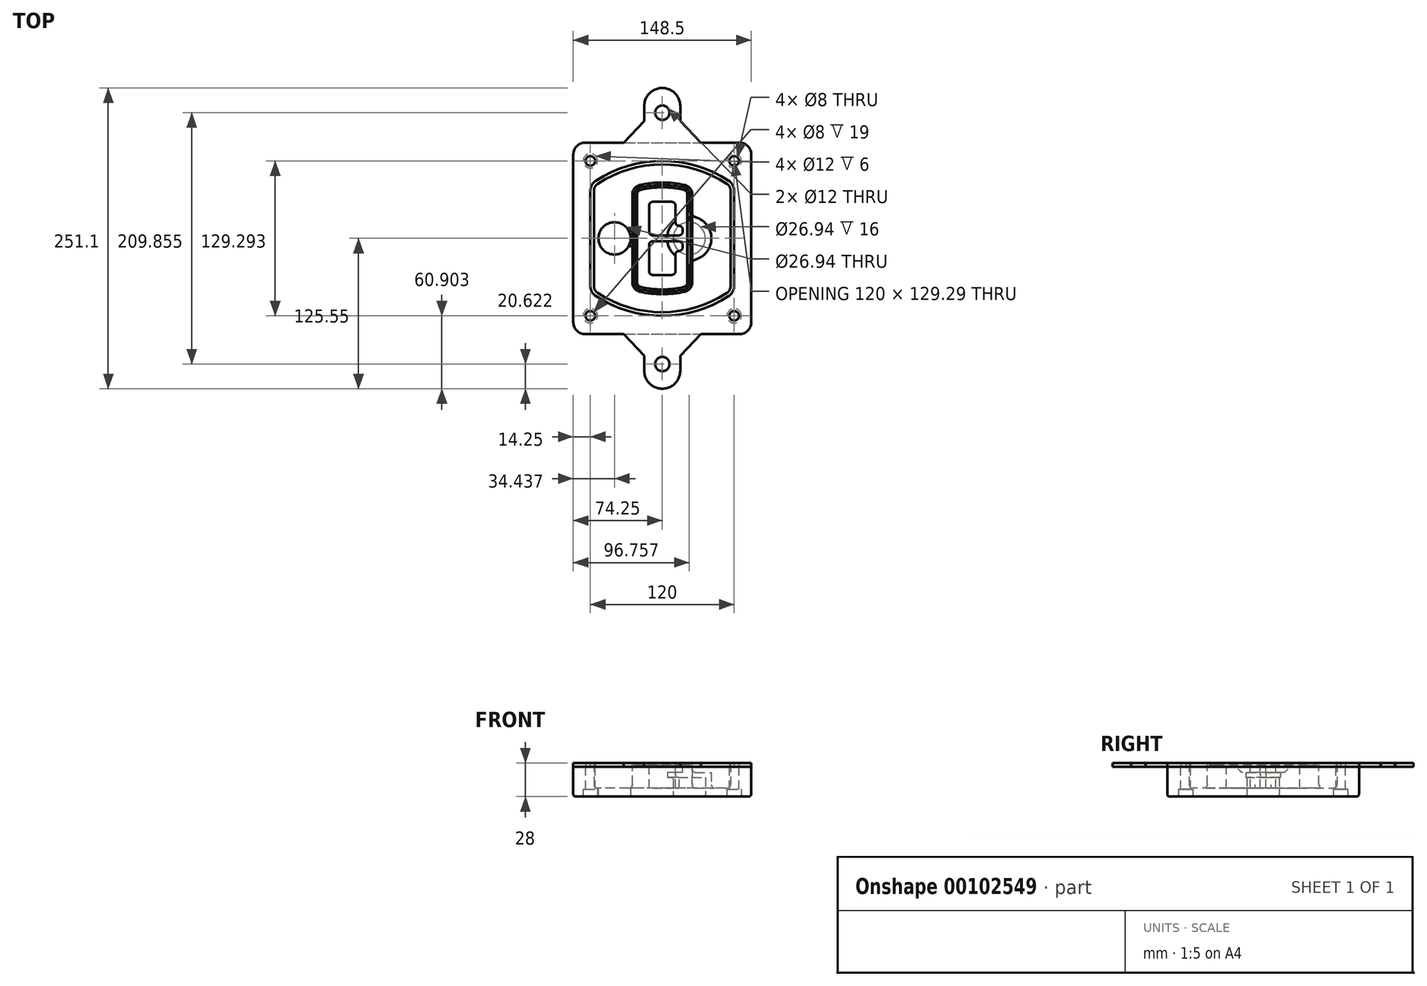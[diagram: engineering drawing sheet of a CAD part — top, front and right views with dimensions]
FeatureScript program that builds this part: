
annotation { "Feature Type Name" : "Feature", "Feature Type Description" : "" }
export const myFeature = defineFeature(function(context is Context, id is Id, definition is map)
    precondition{}
    {
        {
            var Q0;
            Q0=qCreatedBy(makeId("Top.planeOp"),FACE);
            var sketch = newSketch(context, id + "F0", { "sketchPlane" : qUnion([Q0])});
            skPoint(sketch, "E0.rect.middle", {"position": v(0, 0) * mm});
            skLineSegment(sketch, "E1.bottom", {"start": v(-64.25, -80) * mm, "end": v(64.25, -80) * mm});
            skLineSegment(sketch, "E1.top", {"start": v(-64.25, 80) * mm, "end": v(64.25, 80) * mm});
            skLineSegment(sketch, "E1.left", {"start": v(-74.25, -70) * mm, "end": v(-74.25, 70) * mm});
            skLineSegment(sketch, "E1.right", {"start": v(74.25, -70) * mm, "end": v(74.25, 70) * mm});
            skLineSegment(sketch, "E2", {"start": v(-74.25, 80) * mm, "end": v(74.25, -80) * mm, "construction": true});
            skLineSegment(sketch, "E3", {"start": v(74.25, 80) * mm, "end": v(-74.25, -80) * mm, "construction": true});
            skCircle(sketch, "E4", {"center": v(-60, 64.65) * mm, "radius": 4 * mm});
            skCircle(sketch, "E5", {"center": v(60, 64.65) * mm, "radius": 4 * mm});
            skCircle(sketch, "E6", {"center": v(60, -64.65) * mm, "radius": 4 * mm});
            skCircle(sketch, "E7", {"center": v(-60, -64.65) * mm, "radius": 4 * mm});
            skLineSegment(sketch, "E8", {"start": v(-60, 64.65) * mm, "end": v(60, 64.65) * mm, "construction": true});
            skLineSegment(sketch, "E9", {"start": v(60, 64.65) * mm, "end": v(60, -64.65) * mm, "construction": true});
            skLineSegment(sketch, "E10", {"start": v(60, -64.65) * mm, "end": v(-60, -64.65) * mm, "construction": true});
            skLineSegment(sketch, "E11", {"start": v(-60, -64.65) * mm, "end": v(-60, 64.65) * mm, "construction": true});
            skLineSegment(sketch, "E12", {"start": v(-60, 39.77) * mm, "end": v(-60, -39.77) * mm});
            skLineSegment(sketch, "E13", {"start": v(60, 39.77) * mm, "end": v(60, -39.77) * mm});
            skArc(sketch, "E14", {"start": v(55.47, 48.14) * mm, "mid": v(0, 64.65) * mm, "end": v(-55.47, 48.14) * mm});
            skArc(sketch, "E15", {"start": v(-55.47, -48.14) * mm, "mid": v(0, -64.65) * mm, "end": v(55.47, -48.14) * mm});
            skLineSegment(sketch, "E16", {"start": v(-60, 0) * mm, "end": v(60, 0) * mm, "construction": true});
            skPoint(sketch, "E17.visualSharp", {"position": v(-60, -45) * mm});
            skArc(sketch, "E17.filletArc", {"start": v(-60, -39.77) * mm, "mid": v(-58.8, -44.53) * mm, "end": v(-55.47, -48.14) * mm});
            skPoint(sketch, "E18.visualSharp", {"position": v(-60, 45) * mm});
            skArc(sketch, "E18.filletArc", {"start": v(-55.47, 48.14) * mm, "mid": v(-58.8, 44.53) * mm, "end": v(-60, 39.77) * mm});
            skPoint(sketch, "E19.visualSharp", {"position": v(60, 45) * mm});
            skArc(sketch, "E19.filletArc", {"start": v(60, 39.77) * mm, "mid": v(58.8, 44.53) * mm, "end": v(55.47, 48.14) * mm});
            skPoint(sketch, "E20.visualSharp", {"position": v(60, -45) * mm});
            skArc(sketch, "E20.filletArc", {"start": v(55.47, -48.14) * mm, "mid": v(58.8, -44.53) * mm, "end": v(60, -39.77) * mm});
            skPoint(sketch, "E21.visualSharp", {"position": v(-74.25, 80) * mm});
            skArc(sketch, "E21.filletArc", {"start": v(-64.25, 80) * mm, "mid": v(-71.32, 77.07) * mm, "end": v(-74.25, 70) * mm});
            skPoint(sketch, "E22.visualSharp", {"position": v(74.25, 80) * mm});
            skArc(sketch, "E22.filletArc", {"start": v(74.25, 70) * mm, "mid": v(71.32, 77.07) * mm, "end": v(64.25, 80) * mm});
            skPoint(sketch, "E23.visualSharp", {"position": v(74.25, -80) * mm});
            skArc(sketch, "E23.filletArc", {"start": v(64.25, -80) * mm, "mid": v(71.32, -77.07) * mm, "end": v(74.25, -70) * mm});
            skPoint(sketch, "E24.visualSharp", {"position": v(-74.25, -80) * mm});
            skArc(sketch, "E24.filletArc", {"start": v(-74.25, -70) * mm, "mid": v(-71.32, -77.07) * mm, "end": v(-64.25, -80) * mm});
            skArc(sketch, "E25.0", {"start": v(57, 39.77) * mm, "mid": v(56.16, 43.1) * mm, "end": v(53.83, 45.63) * mm});
            skLineSegment(sketch, "E25.1", {"start": v(57, 39.77) * mm, "end": v(57, -39.77) * mm});
            skArc(sketch, "E25.2", {"start": v(53.83, -45.63) * mm, "mid": v(56.16, -43.1) * mm, "end": v(57, -39.77) * mm});
            skArc(sketch, "E25.3", {"start": v(-53.83, -45.63) * mm, "mid": v(0, -61.65) * mm, "end": v(53.83, -45.63) * mm});
            skArc(sketch, "E25.4", {"start": v(-57, -39.77) * mm, "mid": v(-56.16, -43.1) * mm, "end": v(-53.83, -45.63) * mm});
            skArc(sketch, "E25.5", {"start": v(53.83, 45.63) * mm, "mid": v(0, 61.65) * mm, "end": v(-53.83, 45.63) * mm});
            skLineSegment(sketch, "E25.6", {"start": v(-57, 39.77) * mm, "end": v(-57, -39.77) * mm});
            skArc(sketch, "E25.7", {"start": v(-53.83, 45.63) * mm, "mid": v(-56.16, 43.1) * mm, "end": v(-57, 39.77) * mm});
            skArc(sketch, "E26.0", {"start": v(-57.66, 51.49) * mm, "mid": v(-62.31, 46.43) * mm, "end": v(-64, 39.77) * mm});
            skArc(sketch, "E26.1", {"start": v(57.66, 51.49) * mm, "mid": v(0, 68.65) * mm, "end": v(-57.66, 51.49) * mm});
            skArc(sketch, "E26.2", {"start": v(64, 39.77) * mm, "mid": v(62.31, 46.43) * mm, "end": v(57.66, 51.49) * mm});
            skLineSegment(sketch, "E26.3", {"start": v(64, 39.77) * mm, "end": v(64, -39.77) * mm});
            skArc(sketch, "E26.4", {"start": v(57.66, -51.49) * mm, "mid": v(62.31, -46.43) * mm, "end": v(64, -39.77) * mm});
            skLineSegment(sketch, "E26.5", {"start": v(-64, 39.77) * mm, "end": v(-64, -39.77) * mm});
            skArc(sketch, "E26.6", {"start": v(-57.66, -51.49) * mm, "mid": v(0, -68.65) * mm, "end": v(57.66, -51.49) * mm});
            skArc(sketch, "E26.7", {"start": v(-64, -39.77) * mm, "mid": v(-62.31, -46.43) * mm, "end": v(-57.66, -51.49) * mm});
            skSolve(sketch);
        }
        {
            var Q0;
            Q0=makeQuery(id+"F0.imprint","IMPRINT",FACE,{"disambiguationData":[TD([[makeQuery(id+"F0.imprint","IMPRINT",EDGE,{"derivedFrom":sQuery(id+"F0.wireOp",EDGE,"E1.bottom")}),1.0]])]});
            var Q1;
            Q1=makeQuery(id+"F0.imprint","IMPRINT",FACE,{"disambiguationData":[TD([[makeQuery(id+"F0.imprint","IMPRINT",EDGE,{"derivedFrom":sQuery(id+"F0.wireOp",EDGE,"E12")}),1.0]])]});
            var Q2;
            Q2=makeQuery(id+"F0.imprint","IMPRINT",FACE,{"disambiguationData":[TD([[makeQuery(id+"F0.imprint","IMPRINT",EDGE,{"derivedFrom":sQuery(id+"F0.wireOp",EDGE,"E25.0")}),1.0]])]});
            var Q3;
            Q3=makeQuery(id+"F0.imprint","IMPRINT",FACE,{"disambiguationData":[TD([[makeQuery(id+"F0.imprint","IMPRINT",EDGE,{"derivedFrom":sQuery(id+"F0.wireOp",EDGE,"E12")}),-1.0]])]});
            extrude(context, id + "F1", {"entities" : qUnion([Q0, Q1, Q2, Q3]), "oppositeDirection" : true, "depth" : 25 * mm});
        }
        {
            var Q0;
            Q0=makeQuery(id+"F0.imprint","IMPRINT",FACE,{"disambiguationData":[TD([[makeQuery(id+"F0.imprint","IMPRINT",EDGE,{"derivedFrom":sQuery(id+"F0.wireOp",EDGE,"E12")}),1.0]])]});
            extrude(context, id + "F2", {"entities" : qUnion([Q0]), "operationType" : NewBodyOperationType.ADD, "depth" : 3 * mm});
        }
        {
            var Q0;
            Q0=makeQuery(id+"F0.imprint","IMPRINT",FACE,{"disambiguationData":[TD([[makeQuery(id+"F0.imprint","IMPRINT",EDGE,{"derivedFrom":sQuery(id+"F0.wireOp",EDGE,"E25.0")}),1.0]])]});
            extrude(context, id + "F3", {"entities" : qUnion([Q0]), "operationType" : NewBodyOperationType.REMOVE, "oppositeDirection" : true, "depth" : 18 * mm});
        }
        {
            var Q0;
            Q0=makeQuery(id+"F2.opExtrude","CAP_FACE",FACE,{"disambiguationData":[OSD([sQuery(id+"F0.wireOp",EDGE,"E12"),sQuery(id+"F0.wireOp",EDGE,"E13"),sQuery(id+"F0.wireOp",EDGE,"E14"),sQuery(id+"F0.wireOp",EDGE,"E15"),sQuery(id+"F0.wireOp",EDGE,"E17.filletArc"),sQuery(id+"F0.wireOp",EDGE,"E18.filletArc"),sQuery(id+"F0.wireOp",EDGE,"E19.filletArc"),sQuery(id+"F0.wireOp",EDGE,"E20.filletArc"),sQuery(id+"F0.wireOp",EDGE,"E25.0"),sQuery(id+"F0.wireOp",EDGE,"E25.1"),sQuery(id+"F0.wireOp",EDGE,"E25.2"),sQuery(id+"F0.wireOp",EDGE,"E25.3"),sQuery(id+"F0.wireOp",EDGE,"E25.4"),sQuery(id+"F0.wireOp",EDGE,"E25.5"),sQuery(id+"F0.wireOp",EDGE,"E25.6"),sQuery(id+"F0.wireOp",EDGE,"E25.7")])],"isStart":false});
            var sketch = newSketch(context, id + "F4", { "sketchPlane" : qUnion([Q0])});
            skArc(sketch, "E27.0", {"start": v(-18.8, -44.5) * mm, "mid": v(0, -46.65) * mm, "end": v(18.8, -44.5) * mm});
            skArc(sketch, "E28.0", {"start": v(18.8, 44.5) * mm, "mid": v(0, 46.65) * mm, "end": v(-18.8, 44.5) * mm});
            skLineSegment(sketch, "E29", {"start": v(-25, 36.7) * mm, "end": v(-25, -36.7) * mm});
            skLineSegment(sketch, "E30", {"start": v(25, 36.7) * mm, "end": v(25, -36.7) * mm});
            skLineSegment(sketch, "E31", {"start": v(-25, 42.81) * mm, "end": v(25, 42.81) * mm, "construction": true});
            skLineSegment(sketch, "E32", {"start": v(-25, -42.81) * mm, "end": v(25, -42.81) * mm, "construction": true});
            skPoint(sketch, "E33.visualSharp", {"position": v(-25, 42.81) * mm});
            skArc(sketch, "E33.filletArc", {"start": v(-18.8, 44.5) * mm, "mid": v(-23.26, 41.69) * mm, "end": v(-25, 36.7) * mm});
            skPoint(sketch, "E34.visualSharp", {"position": v(25, 42.81) * mm});
            skArc(sketch, "E34.filletArc", {"start": v(25, 36.7) * mm, "mid": v(23.26, 41.69) * mm, "end": v(18.8, 44.5) * mm});
            skPoint(sketch, "E35.visualSharp", {"position": v(25, -42.81) * mm});
            skArc(sketch, "E35.filletArc", {"start": v(18.8, -44.5) * mm, "mid": v(23.26, -41.69) * mm, "end": v(25, -36.7) * mm});
            skPoint(sketch, "E36.visualSharp", {"position": v(-25, -42.81) * mm});
            skArc(sketch, "E36.filletArc", {"start": v(-25, -36.7) * mm, "mid": v(-23.26, -41.69) * mm, "end": v(-18.8, -44.5) * mm});
            skArc(sketch, "E37.0", {"start": v(53.83, 45.63) * mm, "mid": v(0, 61.65) * mm, "end": v(-53.83, 45.63) * mm});
            skArc(sketch, "E37.1", {"start": v(-53.83, 45.63) * mm, "mid": v(-56.16, 43.1) * mm, "end": v(-57, 39.77) * mm});
            skLineSegment(sketch, "E37.2", {"start": v(-57, 39.77) * mm, "end": v(-57, -39.77) * mm});
            skArc(sketch, "E37.3", {"start": v(-57, -39.77) * mm, "mid": v(-56.16, -43.1) * mm, "end": v(-53.83, -45.63) * mm});
            skArc(sketch, "E37.4", {"start": v(-53.83, -45.63) * mm, "mid": v(0, -61.65) * mm, "end": v(53.83, -45.63) * mm});
            skArc(sketch, "E37.5", {"start": v(53.83, -45.63) * mm, "mid": v(56.16, -43.1) * mm, "end": v(57, -39.77) * mm});
            skLineSegment(sketch, "E37.6", {"start": v(57, 39.77) * mm, "end": v(57, -39.77) * mm});
            skArc(sketch, "E37.7", {"start": v(57, 39.77) * mm, "mid": v(56.16, 43.1) * mm, "end": v(53.83, 45.63) * mm});
            skLineSegment(sketch, "E38.0", {"start": v(23, 36.7) * mm, "end": v(23, -36.7) * mm});
            skArc(sketch, "E38.1", {"start": v(18.35, -42.55) * mm, "mid": v(21.7, -40.44) * mm, "end": v(23, -36.7) * mm});
            skArc(sketch, "E38.2", {"start": v(-18.35, -42.55) * mm, "mid": v(0, -44.65) * mm, "end": v(18.35, -42.55) * mm});
            skArc(sketch, "E38.3", {"start": v(-23, -36.7) * mm, "mid": v(-21.7, -40.44) * mm, "end": v(-18.35, -42.55) * mm});
            skLineSegment(sketch, "E38.4", {"start": v(-23, 36.7) * mm, "end": v(-23, -36.7) * mm});
            skArc(sketch, "E38.5", {"start": v(23, 36.7) * mm, "mid": v(21.7, 40.44) * mm, "end": v(18.35, 42.55) * mm});
            skArc(sketch, "E38.6", {"start": v(-18.35, 42.55) * mm, "mid": v(-21.7, 40.44) * mm, "end": v(-23, 36.7) * mm});
            skArc(sketch, "E38.7", {"start": v(18.35, 42.55) * mm, "mid": v(0, 44.65) * mm, "end": v(-18.35, 42.55) * mm});
            skArc(sketch, "E39.0", {"start": v(21, 36.7) * mm, "mid": v(20.13, 39.2) * mm, "end": v(17.9, 40.6) * mm});
            skLineSegment(sketch, "E39.1", {"start": v(21, 36.7) * mm, "end": v(21, -36.7) * mm});
            skArc(sketch, "E39.2", {"start": v(17.9, -40.6) * mm, "mid": v(20.13, -39.2) * mm, "end": v(21, -36.7) * mm});
            skArc(sketch, "E39.3", {"start": v(-17.9, -40.6) * mm, "mid": v(0, -42.65) * mm, "end": v(17.9, -40.6) * mm});
            skArc(sketch, "E39.4", {"start": v(-21, -36.7) * mm, "mid": v(-20.13, -39.2) * mm, "end": v(-17.9, -40.6) * mm});
            skArc(sketch, "E39.5", {"start": v(17.9, 40.6) * mm, "mid": v(0, 42.65) * mm, "end": v(-17.9, 40.6) * mm});
            skLineSegment(sketch, "E39.6", {"start": v(-21, 36.7) * mm, "end": v(-21, -36.7) * mm});
            skArc(sketch, "E39.7", {"start": v(-17.9, 40.6) * mm, "mid": v(-20.13, 39.2) * mm, "end": v(-21, 36.7) * mm});
            skLineSegment(sketch, "E40", {"start": v(-25, 0) * mm, "end": v(25, 0) * mm, "construction": true});
            skLineSegment(sketch, "E41", {"start": v(-11, 5.5) * mm, "end": v(-11, 27.5) * mm});
            skLineSegment(sketch, "E42", {"start": v(-8, 30.5) * mm, "end": v(8, 30.5) * mm});
            skLineSegment(sketch, "E43", {"start": v(11, 27.5) * mm, "end": v(11, 13.5) * mm});
            skLineSegment(sketch, "E44", {"start": v(14, 10.5) * mm, "end": v(14, 10.5) * mm});
            skLineSegment(sketch, "E45", {"start": v(17, 7.5) * mm, "end": v(17, 5.5) * mm});
            skLineSegment(sketch, "E46", {"start": v(14, 2.5) * mm, "end": v(-8, 2.5) * mm});
            skPoint(sketch, "E47.visualSharp", {"position": v(-11, 30.5) * mm});
            skArc(sketch, "E47.filletArc", {"start": v(-8, 30.5) * mm, "mid": v(-10.12, 29.62) * mm, "end": v(-11, 27.5) * mm});
            skPoint(sketch, "E48.visualSharp", {"position": v(11, 30.5) * mm});
            skArc(sketch, "E48.filletArc", {"start": v(11, 27.5) * mm, "mid": v(10.12, 29.62) * mm, "end": v(8, 30.5) * mm});
            skPoint(sketch, "E49.visualSharp", {"position": v(11, 10.5) * mm});
            skArc(sketch, "E49.filletArc", {"start": v(11, 13.5) * mm, "mid": v(11.88, 11.38) * mm, "end": v(14, 10.5) * mm});
            skPoint(sketch, "E50.visualSharp", {"position": v(17, 10.5) * mm});
            skArc(sketch, "E50.filletArc", {"start": v(17, 7.5) * mm, "mid": v(16.12, 9.62) * mm, "end": v(14, 10.5) * mm});
            skPoint(sketch, "E51.visualSharp", {"position": v(17, 2.5) * mm});
            skArc(sketch, "E51.filletArc", {"start": v(14, 2.5) * mm, "mid": v(16.12, 3.38) * mm, "end": v(17, 5.5) * mm});
            skPoint(sketch, "E52.visualSharp", {"position": v(-11, 2.5) * mm});
            skArc(sketch, "E52.filletArc", {"start": v(-11, 5.5) * mm, "mid": v(-10.12, 3.38) * mm, "end": v(-8, 2.5) * mm});
            skLineSegment(sketch, "E53.0.MirrorCS", {"start": v(14, -2.5) * mm, "end": v(-8, -2.5) * mm});
            skArc(sketch, "E54.0.MirrorCS", {"start": v(-11, -5.5) * mm, "mid": v(-10.12, -3.38) * mm, "end": v(-8, -2.5) * mm});
            skLineSegment(sketch, "E55.0.MirrorCS", {"start": v(-11, -5.5) * mm, "end": v(-11, -27.5) * mm});
            skArc(sketch, "E56.0.MirrorCS", {"start": v(-8, -30.5) * mm, "mid": v(-10.12, -29.62) * mm, "end": v(-11, -27.5) * mm});
            skLineSegment(sketch, "E57.0.MirrorCS", {"start": v(-8, -30.5) * mm, "end": v(8, -30.5) * mm});
            skArc(sketch, "E58.0.MirrorCS", {"start": v(11, -27.5) * mm, "mid": v(10.12, -29.62) * mm, "end": v(8, -30.5) * mm});
            skLineSegment(sketch, "E59.0.MirrorCS", {"start": v(11, -27.5) * mm, "end": v(11, -13.5) * mm});
            skArc(sketch, "E60.0.MirrorCS", {"start": v(11, -13.5) * mm, "mid": v(11.88, -11.38) * mm, "end": v(14, -10.5) * mm});
            skArc(sketch, "E61.0.MirrorCS", {"start": v(17, -7.5) * mm, "mid": v(16.12, -9.62) * mm, "end": v(14, -10.5) * mm});
            skLineSegment(sketch, "E62.0.MirrorCS", {"start": v(17, -7.5) * mm, "end": v(17, -5.5) * mm});
            skArc(sketch, "E63.0.MirrorCS", {"start": v(14, -2.5) * mm, "mid": v(16.12, -3.38) * mm, "end": v(17, -5.5) * mm});
            skSolve(sketch);
        }
        {
            var Q0;
            Q0=makeQuery(id+"F4.imprint","IMPRINT",FACE,{"disambiguationData":[TD([[makeQuery(id+"F4.imprint","IMPRINT",EDGE,{"derivedFrom":sQuery(id+"F4.wireOp",EDGE,"E27.0")}),1.0]])]});
            var Q1;
            Q1=makeQuery(id+"F4.imprint","IMPRINT",FACE,{"disambiguationData":[TD([[makeQuery(id+"F4.imprint","IMPRINT",EDGE,{"derivedFrom":sQuery(id+"F4.wireOp",EDGE,"E38.0")}),-1.0]])]});
            var Q2;
            Q2=makeQuery(id+"F4.imprint","IMPRINT",FACE,{"disambiguationData":[TD([[makeQuery(id+"F4.imprint","IMPRINT",EDGE,{"derivedFrom":sQuery(id+"F4.wireOp",EDGE,"E39.0")}),1.0]])]});
            extrude(context, id + "F5", {"entities" : qUnion([Q0, Q1, Q2]), "operationType" : NewBodyOperationType.ADD, "endBound" : BoundingType.UP_TO_NEXT, "oppositeDirection" : true, "depth" : 25 * mm});
        }
        {
            var Q0;
            Q0=makeQuery(id+"F4.imprint","IMPRINT",FACE,{"disambiguationData":[TD([[makeQuery(id+"F4.imprint","IMPRINT",EDGE,{"derivedFrom":sQuery(id+"F4.wireOp",EDGE,"E38.0")}),-1.0]])]});
            extrude(context, id + "F6", {"entities" : qUnion([Q0]), "operationType" : NewBodyOperationType.REMOVE, "oppositeDirection" : true, "depth" : 2 * mm});
        }
        {
            var Q0;
            Q0=makeQuery(id+"F1.opExtrude","CAP_FACE",FACE,{"disambiguationData":[OSD([sQuery(id+"F0.wireOp",EDGE,"E1.bottom"),sQuery(id+"F0.wireOp",EDGE,"E1.top"),sQuery(id+"F0.wireOp",EDGE,"E1.left"),sQuery(id+"F0.wireOp",EDGE,"E1.right"),sQuery(id+"F0.wireOp",EDGE,"E4"),sQuery(id+"F0.wireOp",EDGE,"E5"),sQuery(id+"F0.wireOp",EDGE,"E6"),sQuery(id+"F0.wireOp",EDGE,"E7"),sQuery(id+"F0.wireOp",EDGE,"E21.filletArc"),sQuery(id+"F0.wireOp",EDGE,"E22.filletArc"),sQuery(id+"F0.wireOp",EDGE,"E23.filletArc"),sQuery(id+"F0.wireOp",EDGE,"E24.filletArc")])],"isStart":false});
            var sketch = newSketch(context, id + "F7", { "sketchPlane" : qUnion([Q0])});
            skCircle(sketch, "E64", {"center": v(22.5, 0) * mm, "radius": 13.47 * mm});
            skCircle(sketch, "E65", {"center": v(-39.81, 0) * mm, "radius": 13.47 * mm});
            skLineSegment(sketch, "E66", {"start": v(74.25, 0) * mm, "end": v(-74.25, 0) * mm});
            skCircle(sketch, "E67", {"center": v(22.5, 0) * mm, "radius": 18.47 * mm});
            skCircle(sketch, "E68", {"center": v(60, -64.65) * mm, "radius": 6 * mm});
            skCircle(sketch, "E69", {"center": v(-60, -64.65) * mm, "radius": 6 * mm});
            skCircle(sketch, "E70", {"center": v(-60, 64.65) * mm, "radius": 6 * mm});
            skCircle(sketch, "E71", {"center": v(60, 64.65) * mm, "radius": 6 * mm});
            skSolve(sketch);
        }
        {
            var Q0;
            {var subQ1=sQuery(id+"F7.wireOp",EDGE,"E66");var subQ4=sQuery(id+"F7.wireOp",EDGE,"E64");var subQ6=makeQuery(id+"F7.imprint","INTERSECT",VERTEX,{"disambiguationData":[OD(0.0)],"derivedFrom":[subQ4,subQ1]});Q0=makeQuery(id+"F7.imprint","IMPRINT",FACE,{"disambiguationData":[TD([[makeQuery(id+"F7.imprint","IMPRINT",EDGE,{"disambiguationData":[TD([[subQ6,-1.0]])],"derivedFrom":subQ4}),-1.0]])]});}
            var Q1;
            {var subQ0=sQuery(id+"F7.wireOp",EDGE,"E66");var subQ1=sQuery(id+"F7.wireOp",EDGE,"E64");var subQ3=makeQuery(id+"F7.imprint","INTERSECT",VERTEX,{"disambiguationData":[OD(0.0)],"derivedFrom":[subQ1,subQ0]});Q1=makeQuery(id+"F7.imprint","IMPRINT",FACE,{"disambiguationData":[TD([[makeQuery(id+"F7.imprint","IMPRINT",EDGE,{"disambiguationData":[TD([[subQ3,-1.0]])],"derivedFrom":subQ1}),1.0]])]});}
            var Q2;
            {var subQ0=sQuery(id+"F7.wireOp",EDGE,"E66");var subQ1=sQuery(id+"F7.wireOp",EDGE,"E64");var subQ3=makeQuery(id+"F7.imprint","INTERSECT",VERTEX,{"disambiguationData":[OD(0.0)],"derivedFrom":[subQ1,subQ0]});Q2=makeQuery(id+"F7.imprint","IMPRINT",FACE,{"disambiguationData":[TD([[makeQuery(id+"F7.imprint","IMPRINT",EDGE,{"disambiguationData":[TD([[subQ3,1.0]])],"derivedFrom":subQ1}),1.0]])]});}
            var Q3;
            {var subQ1=sQuery(id+"F7.wireOp",EDGE,"E66");var subQ4=sQuery(id+"F7.wireOp",EDGE,"E64");var subQ6=makeQuery(id+"F7.imprint","INTERSECT",VERTEX,{"disambiguationData":[OD(0.0)],"derivedFrom":[subQ4,subQ1]});Q3=makeQuery(id+"F7.imprint","IMPRINT",FACE,{"disambiguationData":[TD([[makeQuery(id+"F7.imprint","IMPRINT",EDGE,{"disambiguationData":[TD([[subQ6,1.0]])],"derivedFrom":subQ4}),-1.0]])]});}
            extrude(context, id + "F8", {"entities" : qUnion([Q0, Q1, Q2, Q3]), "operationType" : NewBodyOperationType.ADD, "oppositeDirection" : true, "depth" : 20 * mm});
        }
        {
            var Q0;
            {var subQ0=sQuery(id+"F7.wireOp",EDGE,"E66");var subQ1=sQuery(id+"F7.wireOp",EDGE,"E64");var subQ3=makeQuery(id+"F7.imprint","INTERSECT",VERTEX,{"disambiguationData":[OD(0.0)],"derivedFrom":[subQ1,subQ0]});Q0=makeQuery(id+"F7.imprint","IMPRINT",FACE,{"disambiguationData":[TD([[makeQuery(id+"F7.imprint","IMPRINT",EDGE,{"disambiguationData":[TD([[subQ3,-1.0]])],"derivedFrom":subQ1}),1.0]])]});}
            var Q1;
            {var subQ0=sQuery(id+"F7.wireOp",EDGE,"E66");var subQ1=sQuery(id+"F7.wireOp",EDGE,"E64");var subQ3=makeQuery(id+"F7.imprint","INTERSECT",VERTEX,{"disambiguationData":[OD(0.0)],"derivedFrom":[subQ1,subQ0]});Q1=makeQuery(id+"F7.imprint","IMPRINT",FACE,{"disambiguationData":[TD([[makeQuery(id+"F7.imprint","IMPRINT",EDGE,{"disambiguationData":[TD([[subQ3,1.0]])],"derivedFrom":subQ1}),1.0]])]});}
            extrude(context, id + "F9", {"entities" : qUnion([Q0, Q1]), "operationType" : NewBodyOperationType.REMOVE, "oppositeDirection" : true, "depth" : 16 * mm});
        }
        {
            var Q0;
            {var subQ0=sQuery(id+"F7.wireOp",EDGE,"E66");var subQ1=sQuery(id+"F7.wireOp",EDGE,"E65");var subQ3=makeQuery(id+"F7.imprint","INTERSECT",VERTEX,{"disambiguationData":[OD(0.0)],"derivedFrom":[subQ1,subQ0]});Q0=makeQuery(id+"F7.imprint","IMPRINT",FACE,{"disambiguationData":[TD([[makeQuery(id+"F7.imprint","IMPRINT",EDGE,{"disambiguationData":[TD([[subQ3,-1.0]])],"derivedFrom":subQ1}),1.0]])]});}
            var Q1;
            {var subQ0=sQuery(id+"F7.wireOp",EDGE,"E66");var subQ1=sQuery(id+"F7.wireOp",EDGE,"E65");var subQ3=makeQuery(id+"F7.imprint","INTERSECT",VERTEX,{"disambiguationData":[OD(0.0)],"derivedFrom":[subQ1,subQ0]});Q1=makeQuery(id+"F7.imprint","IMPRINT",FACE,{"disambiguationData":[TD([[makeQuery(id+"F7.imprint","IMPRINT",EDGE,{"disambiguationData":[TD([[subQ3,1.0]])],"derivedFrom":subQ1}),1.0]])]});}
            extrude(context, id + "F10", {"entities" : qUnion([Q0, Q1]), "operationType" : NewBodyOperationType.REMOVE, "oppositeDirection" : true, "depth" : 25 * mm});
        }
        {
            var Q0;
            Q0=makeQuery(id+"F7.imprint","IMPRINT",FACE,{"disambiguationData":[TD([[makeQuery(id+"F7.imprint","IMPRINT",EDGE,{"derivedFrom":sQuery(id+"F7.wireOp",EDGE,"E68")}),1.0]])]});
            var Q1;
            Q1=makeQuery(id+"F7.imprint","IMPRINT",FACE,{"disambiguationData":[TD([[makeQuery(id+"F7.imprint","IMPRINT",EDGE,{"derivedFrom":makeQuery(id+"F1.opExtrude","CAP_EDGE",EDGE,{"disambiguationData":[OSD([sQuery(id+"F0.wireOp",EDGE,"E5")])],"isStart":false})}),-1.0]])]});
            var Q2;
            Q2=makeQuery(id+"F7.imprint","IMPRINT",FACE,{"disambiguationData":[TD([[makeQuery(id+"F7.imprint","IMPRINT",EDGE,{"derivedFrom":sQuery(id+"F7.wireOp",EDGE,"E69")}),1.0]])]});
            var Q3;
            Q3=makeQuery(id+"F7.imprint","IMPRINT",FACE,{"disambiguationData":[TD([[makeQuery(id+"F7.imprint","IMPRINT",EDGE,{"derivedFrom":makeQuery(id+"F1.opExtrude","CAP_EDGE",EDGE,{"disambiguationData":[OSD([sQuery(id+"F0.wireOp",EDGE,"E4")])],"isStart":false})}),-1.0]])]});
            var Q4;
            Q4=makeQuery(id+"F7.imprint","IMPRINT",FACE,{"disambiguationData":[TD([[makeQuery(id+"F7.imprint","IMPRINT",EDGE,{"derivedFrom":sQuery(id+"F7.wireOp",EDGE,"E70")}),1.0]])]});
            var Q5;
            Q5=makeQuery(id+"F7.imprint","IMPRINT",FACE,{"disambiguationData":[TD([[makeQuery(id+"F7.imprint","IMPRINT",EDGE,{"derivedFrom":makeQuery(id+"F1.opExtrude","CAP_EDGE",EDGE,{"disambiguationData":[OSD([sQuery(id+"F0.wireOp",EDGE,"E7")])],"isStart":false})}),-1.0]])]});
            var Q6;
            Q6=makeQuery(id+"F7.imprint","IMPRINT",FACE,{"disambiguationData":[TD([[makeQuery(id+"F7.imprint","IMPRINT",EDGE,{"derivedFrom":sQuery(id+"F7.wireOp",EDGE,"E71")}),1.0]])]});
            var Q7;
            Q7=makeQuery(id+"F7.imprint","IMPRINT",FACE,{"disambiguationData":[TD([[makeQuery(id+"F7.imprint","IMPRINT",EDGE,{"derivedFrom":makeQuery(id+"F1.opExtrude","CAP_EDGE",EDGE,{"disambiguationData":[OSD([sQuery(id+"F0.wireOp",EDGE,"E6")])],"isStart":false})}),-1.0]])]});
            extrude(context, id + "F11", {"entities" : qUnion([Q0, Q1, Q2, Q3, Q4, Q5, Q6, Q7]), "operationType" : NewBodyOperationType.REMOVE, "oppositeDirection" : true, "depth" : 6 * mm});
        }
        {
            var Q0;
            Q0=makeQuery(id+"F9.boolean.opBoolean","COPY",FACE,{"derivedFrom":makeQuery(id+"F9.opExtrude","CAP_FACE",FACE,{"disambiguationData":[OSD([sQuery(id+"F7.wireOp",EDGE,"E64")])],"isStart":false})});
            var sketch = newSketch(context, id + "F12", { "sketchPlane" : qUnion([Q0])});
            skArc(sketch, "E72.0", {"start": v(11, 14.45) * mm, "mid": v(6.45, 9.13) * mm, "end": v(4.2, 2.5) * mm});
            skArc(sketch, "E72.1", {"start": v(4.2, -2.5) * mm, "mid": v(6.45, -9.13) * mm, "end": v(11, -14.45) * mm});
            skLineSegment(sketch, "E73", {"start": v(4.2, -2.5) * mm, "end": v(14, -2.5) * mm});
            skLineSegment(sketch, "E74.0", {"start": v(14, 2.5) * mm, "end": v(4.2, 2.5) * mm});
            skArc(sketch, "E74.1", {"start": v(14, 2.5) * mm, "mid": v(16.12, 3.38) * mm, "end": v(17, 5.5) * mm});
            skLineSegment(sketch, "E74.2", {"start": v(17, 7.5) * mm, "end": v(17, 5.5) * mm});
            skArc(sketch, "E74.3", {"start": v(17, 7.5) * mm, "mid": v(16.12, 9.62) * mm, "end": v(14, 10.5) * mm});
            skArc(sketch, "E74.4", {"start": v(11, 13.5) * mm, "mid": v(11.88, 11.38) * mm, "end": v(14, 10.5) * mm});
            skLineSegment(sketch, "E74.5", {"start": v(11, 14.45) * mm, "end": v(11, 13.5) * mm});
            skLineSegment(sketch, "E74.7", {"start": v(14, -2.5) * mm, "end": v(4.2, -2.5) * mm});
            skArc(sketch, "E74.8", {"start": v(14, -2.5) * mm, "mid": v(16.12, -3.38) * mm, "end": v(17, -5.5) * mm});
            skLineSegment(sketch, "E74.9", {"start": v(17, -7.5) * mm, "end": v(17, -5.5) * mm});
            skArc(sketch, "E74.10", {"start": v(17, -7.5) * mm, "mid": v(16.12, -9.62) * mm, "end": v(14, -10.5) * mm});
            skArc(sketch, "E74.11", {"start": v(11, -13.5) * mm, "mid": v(11.88, -11.38) * mm, "end": v(14, -10.5) * mm});
            skLineSegment(sketch, "E74.12", {"start": v(11, -14.45) * mm, "end": v(11, -13.5) * mm});
            skPoint(sketch, "E75.orphan", {"position": v(11, -27.5) * mm});
            skPoint(sketch, "E76.orphan", {"position": v(-8, -2.5) * mm});
            skPoint(sketch, "E77.orphan", {"position": v(-8, 2.5) * mm});
            skPoint(sketch, "E78.orphan", {"position": v(11, 27.5) * mm});
            skSolve(sketch);
        }
        {
            var Q0;
            {var subQ7=sQuery(id+"F12.wireOp",EDGE,"E72.0");var subQ14=sQuery(id+"F12.wireOp",EDGE,"E72.1");var subQ16=sQuery(id+"F12.wireOp",EDGE,"E74.1");var subQ18=sQuery(id+"F12.wireOp",EDGE,"E74.8");Q0=qUnion([makeQuery(id+"F12.imprint","IMPRINT",FACE,{"disambiguationData":[TD([[makeQuery(id+"F12.imprint","IMPRINT",EDGE,{"derivedFrom":subQ7}),1.0]])]}),makeQuery(id+"F12.imprint","IMPRINT",FACE,{"disambiguationData":[TD([[makeQuery(id+"F12.imprint","IMPRINT",EDGE,{"derivedFrom":subQ14}),1.0]])]}),makeQuery(id+"F12.imprint","IMPRINT",FACE,{"disambiguationData":[TD([[makeQuery(id+"F12.imprint","IMPRINT",EDGE,{"derivedFrom":subQ16}),1.0]])]}),makeQuery(id+"F12.imprint","IMPRINT",FACE,{"disambiguationData":[TD([[makeQuery(id+"F12.imprint","IMPRINT",EDGE,{"derivedFrom":subQ18}),-1.0]])]})]);}
            var Q1;
            Q1 = qSketchRegion(id + "F16", true);
            var Q2;
            Q2=makeQuery(id+"F5.boolean.opBoolean","SPLIT",FACE,{"disambiguationData":[TD([makeQuery(id+"F5.opExtrude","SWEPT_FACE",FACE,{"disambiguationData":[OSD([sQuery(id+"F4.wireOp",EDGE,"E41")])]})])],"derivedFrom":makeQuery(id+"F3.boolean.opBoolean","COPY",FACE,{"derivedFrom":makeQuery(id+"F3.opExtrude","CAP_FACE",FACE,{"disambiguationData":[OSD([sQuery(id+"F0.wireOp",EDGE,"E25.0"),sQuery(id+"F0.wireOp",EDGE,"E25.1"),sQuery(id+"F0.wireOp",EDGE,"E25.2"),sQuery(id+"F0.wireOp",EDGE,"E25.3"),sQuery(id+"F0.wireOp",EDGE,"E25.4"),sQuery(id+"F0.wireOp",EDGE,"E25.5"),sQuery(id+"F0.wireOp",EDGE,"E25.6"),sQuery(id+"F0.wireOp",EDGE,"E25.7")])],"isStart":false})})});
            extrude(context, id + "F13", {"entities" : qUnion([Q0, Q1]), "operationType" : NewBodyOperationType.REMOVE, "endBound" : BoundingType.UP_TO_SURFACE, "endBoundEntityFace" : qUnion([Q2]), "depth" : 25 * mm});
        }
        {
            var Q0;
            Q0=makeQuery(id+"F3.boolean.opBoolean","COPY",EDGE,{"derivedFrom":makeQuery(id+"F3.opExtrude","CAP_EDGE",EDGE,{"disambiguationData":[OSD([sQuery(id+"F0.wireOp",EDGE,"E25.6")])],"isStart":false})});
            var Q1;
            Q1=makeQuery(id+"F8.boolean.opBoolean","INTERSECT",EDGE,{"derivedFrom":[makeQuery(id+"F5.opExtrude","SWEPT_FACE",FACE,{"disambiguationData":[OSD([sQuery(id+"F4.wireOp",EDGE,"E30")])]}),makeQuery(id+"F8.opExtrude","CAP_FACE",FACE,{"disambiguationData":[OSD([sQuery(id+"F7.wireOp",EDGE,"E67")])],"isStart":false})]});
            var Q2;
            Q2=makeQuery(id+"F8.boolean.opBoolean","INTERSECT",EDGE,{"disambiguationData":[OD(1.0)],"derivedFrom":[makeQuery(id+"F5.opExtrude","SWEPT_FACE",FACE,{"disambiguationData":[OSD([sQuery(id+"F4.wireOp",EDGE,"E30")])]}),makeQuery(id+"F8.opExtrude","SWEPT_FACE",FACE,{"disambiguationData":[OSD([sQuery(id+"F7.wireOp",EDGE,"E67")])]})]});
            var Q3;
            {var subQ0=sQuery(id+"F4.wireOp",EDGE,"E30");Q3=makeQuery(id+"F8.boolean.opBoolean","SPLIT",EDGE,{"disambiguationData":[TD([makeQuery(id+"F5.opExtrude","SWEPT_FACE",FACE,{"disambiguationData":[OSD([sQuery(id+"F4.wireOp",EDGE,"E35.filletArc")])]})])],"derivedFrom":makeQuery(id+"F5.opExtrude","CAP_EDGE",EDGE,{"disambiguationData":[OSD([subQ0])],"isStart":false})});}
            var Q4;
            {var subQ0=sQuery(id+"F0.wireOp",EDGE,"E25.7");var subQ1=sQuery(id+"F0.wireOp",EDGE,"E25.1");var subQ2=sQuery(id+"F0.wireOp",EDGE,"E25.6");var subQ3=sQuery(id+"F0.wireOp",EDGE,"E25.5");var subQ4=sQuery(id+"F0.wireOp",EDGE,"E25.4");var subQ5=sQuery(id+"F0.wireOp",EDGE,"E25.0");var subQ6=sQuery(id+"F0.wireOp",EDGE,"E25.2");var subQ7=sQuery(id+"F0.wireOp",EDGE,"E25.3");Q4=makeQuery(id+"F8.boolean.opBoolean","INTERSECT",EDGE,{"derivedFrom":[makeQuery(id+"F5.boolean.opBoolean","SPLIT",FACE,{"disambiguationData":[TD([makeQuery(id+"F2.opExtrude","SWEPT_FACE",FACE,{"disambiguationData":[OSD([subQ5])]})])],"derivedFrom":makeQuery(id+"F3.boolean.opBoolean","COPY",FACE,{"derivedFrom":makeQuery(id+"F3.opExtrude","CAP_FACE",FACE,{"disambiguationData":[OSD([subQ5,subQ1,subQ6,subQ7,subQ4,subQ3,subQ2,subQ0])],"isStart":false})})}),makeQuery(id+"F8.opExtrude","SWEPT_FACE",FACE,{"disambiguationData":[OSD([sQuery(id+"F7.wireOp",EDGE,"E67")])]})]});}
            var Q5;
            Q5=makeQuery(id+"F8.boolean.opBoolean","INTERSECT",EDGE,{"disambiguationData":[OD(0.0)],"derivedFrom":[makeQuery(id+"F5.opExtrude","SWEPT_FACE",FACE,{"disambiguationData":[OSD([sQuery(id+"F4.wireOp",EDGE,"E30")])]}),makeQuery(id+"F8.opExtrude","SWEPT_FACE",FACE,{"disambiguationData":[OSD([sQuery(id+"F7.wireOp",EDGE,"E67")])]})]});
            fillet(context, id + "F14", {"entities" : qUnion([Q0, Q1, Q2, Q3, Q4, Q5]), "radius" : 3 * mm, "tangentPropagation" : true, "allowEdgeOverflow" : false});
        }
        {
            var Q0;
            Q0=makeQuery(id+"F1.opExtrude","CAP_EDGE",EDGE,{"disambiguationData":[OSD([sQuery(id+"F0.wireOp",EDGE,"E1.bottom")])],"isStart":false});
            fillet(context, id + "F15", {"entities" : qUnion([Q0]), "radius" : 2 * mm, "tangentPropagation" : true, "allowEdgeOverflow" : false});
        }
        {
            var Q0;
            {var subQ0=sQuery(id+"F0.wireOp",EDGE,"E22.filletArc");var subQ1=sQuery(id+"F0.wireOp",EDGE,"E7");var subQ2=sQuery(id+"F0.wireOp",EDGE,"E6");var subQ3=sQuery(id+"F0.wireOp",EDGE,"E5");var subQ4=sQuery(id+"F0.wireOp",EDGE,"E4");var subQ5=sQuery(id+"F0.wireOp",EDGE,"E1.bottom");var subQ6=sQuery(id+"F0.wireOp",EDGE,"E21.filletArc");var subQ7=sQuery(id+"F0.wireOp",EDGE,"E1.top");var subQ8=sQuery(id+"F0.wireOp",EDGE,"E1.left");var subQ9=sQuery(id+"F0.wireOp",EDGE,"E1.right");var subQ10=sQuery(id+"F0.wireOp",EDGE,"E23.filletArc");var subQ11=sQuery(id+"F0.wireOp",EDGE,"E24.filletArc");Q0=makeQuery(id+"F2.boolean.opBoolean","SPLIT",FACE,{"disambiguationData":[TD([makeQuery(id+"F1.opExtrude","SWEPT_FACE",FACE,{"disambiguationData":[OSD([subQ5])]})])],"derivedFrom":makeQuery(id+"F1.opExtrude","CAP_FACE",FACE,{"disambiguationData":[OSD([subQ5,subQ7,subQ8,subQ9,subQ4,subQ3,subQ2,subQ1,subQ6,subQ0,subQ10,subQ11])],"isStart":true})});}
            var sketch = newSketch(context, id + "F16", { "sketchPlane" : qUnion([Q0])});
            skLineSegment(sketch, "E79", {"start": v(0, 80) * mm, "end": v(0, 104.93) * mm, "construction": true});
            skLineSegment(sketch, "E80", {"start": v(-32.3, 80) * mm, "end": v(-15, 98) * mm});
            skLineSegment(sketch, "E81", {"start": v(-15, 98) * mm, "end": v(-15, 110) * mm});
            skLineSegment(sketch, "E82", {"start": v(32.3, 80) * mm, "end": v(14.99, 98) * mm});
            skLineSegment(sketch, "E83", {"start": v(14.99, 98) * mm, "end": v(14.99, 110) * mm});
            skArc(sketch, "E84", {"start": v(14.99, 110) * mm, "mid": v(0, 125.55) * mm, "end": v(-15, 110) * mm});
            skCircle(sketch, "E85", {"center": v(0, 104.93) * mm, "radius": 6 * mm});
            skLineSegment(sketch, "E86", {"start": v(0, 0) * mm, "end": v(-74.25, 0) * mm, "construction": true});
            skLineSegment(sketch, "E87", {"start": v(-74.25, 0) * mm, "end": v(74.25, 0) * mm, "construction": true});
            skLineSegment(sketch, "E88.MirrorCS", {"start": v(-32.3, -80) * mm, "end": v(-15, -98) * mm});
            skLineSegment(sketch, "E89.MirrorCS", {"start": v(-15, -98) * mm, "end": v(-15, -110) * mm});
            skArc(sketch, "E90.MirrorCS", {"start": v(14.99, -110) * mm, "mid": v(0, -125.55) * mm, "end": v(-15, -110) * mm});
            skLineSegment(sketch, "E91.MirrorCS", {"start": v(14.99, -98) * mm, "end": v(14.99, -110) * mm});
            skLineSegment(sketch, "E92.MirrorCS", {"start": v(32.3, -80) * mm, "end": v(14.99, -98) * mm});
            skCircle(sketch, "E93.MirrorC", {"center": v(0, -104.93) * mm, "radius": 6 * mm});
            skLineSegment(sketch, "E94.MirrorCS", {"start": v(0, -80) * mm, "end": v(0, -104.93) * mm, "construction": true});
            skSolve(sketch);
        }
        {
            var Q0;
            {var subQ1=sQuery(id+"F16.wireOp",EDGE,"E80");Q0=makeQuery(id+"F16.imprint","IMPRINT",FACE,{"disambiguationData":[TD([[makeQuery(id+"F16.imprint","IMPRINT",EDGE,{"derivedFrom":subQ1}),-1.0]])]});}
            var Q1;
            Q1=makeQuery(id+"F16.imprint","IMPRINT",FACE,{"disambiguationData":[TD([[makeQuery(id+"F16.imprint","IMPRINT",EDGE,{"derivedFrom":makeQuery(id+"F1.opExtrude","CAP_EDGE",EDGE,{"disambiguationData":[OSD([sQuery(id+"F0.wireOp",EDGE,"E1.left")])],"isStart":true})}),-1.0]])]});
            var Q2;
            {var subQ0=sQuery(id+"F16.wireOp",EDGE,"E88.MirrorCS");Q2=makeQuery(id+"F16.imprint","IMPRINT",FACE,{"disambiguationData":[TD([[makeQuery(id+"F16.imprint","IMPRINT",EDGE,{"derivedFrom":subQ0}),1.0]])]});}
            var Q3;
            Q3=makeQuery(id+"F2.opExtrude","CAP_FACE",FACE,{"disambiguationData":[OSD([sQuery(id+"F0.wireOp",EDGE,"E12"),sQuery(id+"F0.wireOp",EDGE,"E13"),sQuery(id+"F0.wireOp",EDGE,"E14"),sQuery(id+"F0.wireOp",EDGE,"E15"),sQuery(id+"F0.wireOp",EDGE,"E17.filletArc"),sQuery(id+"F0.wireOp",EDGE,"E18.filletArc"),sQuery(id+"F0.wireOp",EDGE,"E19.filletArc"),sQuery(id+"F0.wireOp",EDGE,"E20.filletArc"),sQuery(id+"F0.wireOp",EDGE,"E25.0"),sQuery(id+"F0.wireOp",EDGE,"E25.1"),sQuery(id+"F0.wireOp",EDGE,"E25.2"),sQuery(id+"F0.wireOp",EDGE,"E25.3"),sQuery(id+"F0.wireOp",EDGE,"E25.4"),sQuery(id+"F0.wireOp",EDGE,"E25.5"),sQuery(id+"F0.wireOp",EDGE,"E25.6"),sQuery(id+"F0.wireOp",EDGE,"E25.7")])],"isStart":false});
            extrude(context, id + "F17", {"entities" : qUnion([Q0, Q1, Q2]), "endBound" : BoundingType.UP_TO_SURFACE, "endBoundEntityFace" : qUnion([Q3]), "depth" : 25 * mm});
        }
    });
